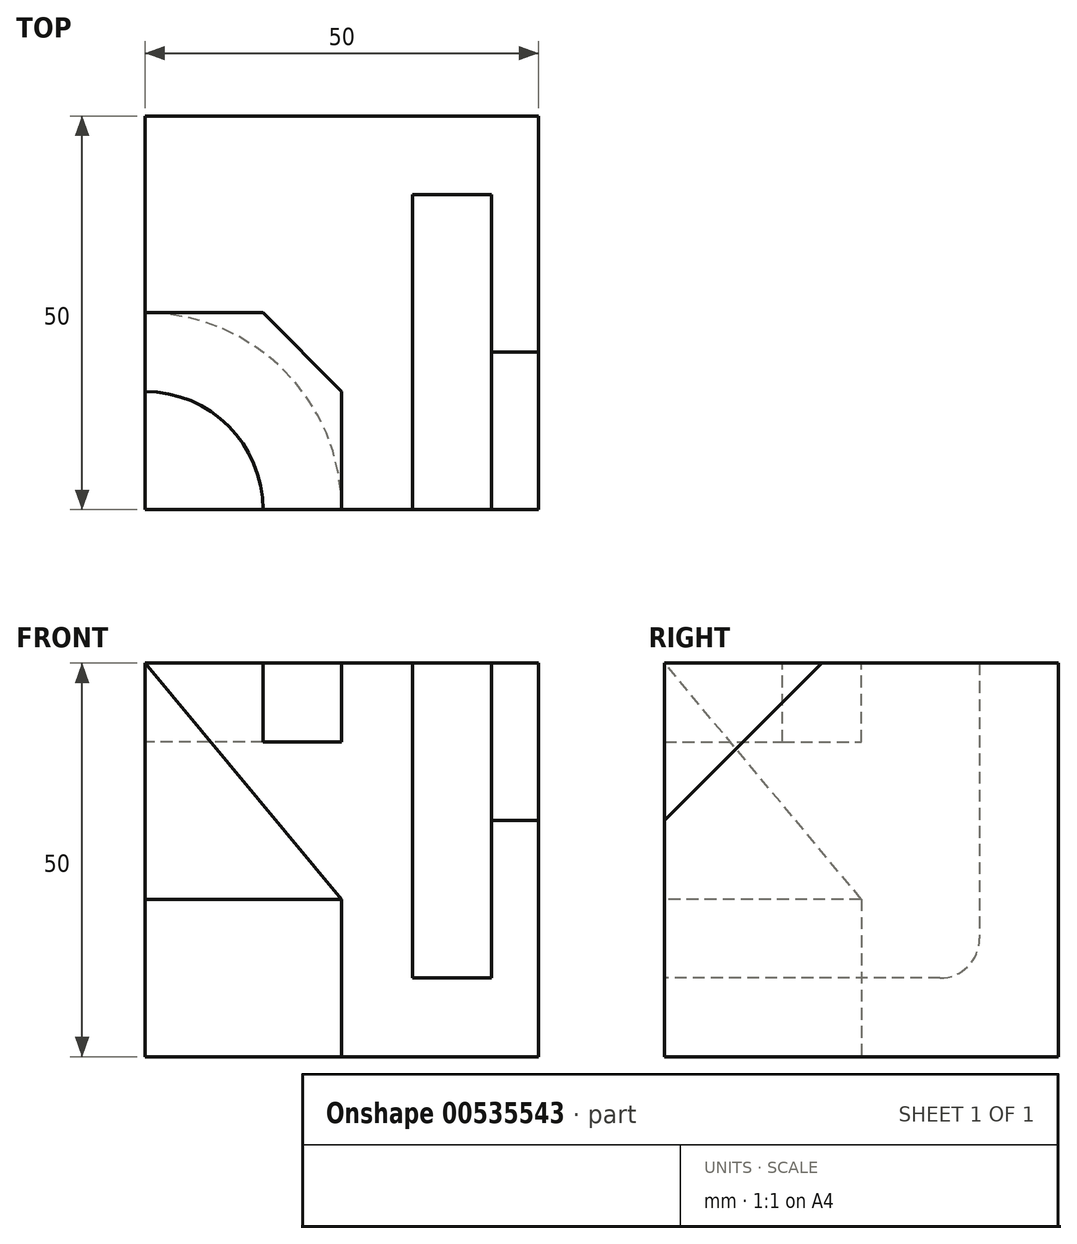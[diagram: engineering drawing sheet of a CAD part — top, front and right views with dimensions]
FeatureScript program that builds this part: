
annotation { "Feature Type Name" : "Feature", "Feature Type Description" : "" }
export const myFeature = defineFeature(function(context is Context, id is Id, definition is map)
    precondition{}
    {
        {
            var Q0;
            Q0=qCreatedBy(makeId("Front.planeOp"),FACE);
            var sketch = newSketch(context, id + "F0", { "sketchPlane" : qUnion([Q0])});
            skLineSegment(sketch, "E0.bottom", {"start": v(0, 0) * mm, "end": v(-50, 0) * mm});
            skLineSegment(sketch, "E0.top", {"start": v(0, 50) * mm, "end": v(-50, 50) * mm});
            skLineSegment(sketch, "E0.left", {"start": v(0, 0) * mm, "end": v(0, 50) * mm});
            skLineSegment(sketch, "E0.right", {"start": v(-50, 0) * mm, "end": v(-50, 50) * mm});
            skSolve(sketch);
        }
        {
            var Q0;
            Q0=makeQuery(id+"F0.imprint","IMPRINT",FACE,{"disambiguationData":[TD([[makeQuery(id+"F0.imprint","IMPRINT",EDGE,{"derivedFrom":sQuery(id+"F0.wireOp",EDGE,"E0.bottom")}),-1.0]])]});
            extrude(context, id + "F1", {"entities" : qUnion([Q0]), "depth" : 50 * mm, "offsetDistance" : 25 * mm});
        }
        {
            var Q0;
            Q0=makeQuery(id+"F1.opExtrude","SWEPT_FACE",FACE,{"disambiguationData":[OSD([sQuery(id+"F0.wireOp",EDGE,"E0.top")])]});
            var sketch = newSketch(context, id + "F2", { "sketchPlane" : qUnion([Q0])});
            skLineSegment(sketch, "E1", {"start": v(-50, -50) * mm, "end": v(-25, -50) * mm});
            skLineSegment(sketch, "E2", {"start": v(-25, -50) * mm, "end": v(-25, -35) * mm});
            skLineSegment(sketch, "E3", {"start": v(-25, -35) * mm, "end": v(-35, -25) * mm});
            skLineSegment(sketch, "E4", {"start": v(-35, -25) * mm, "end": v(-50, -25) * mm});
            skLineSegment(sketch, "E5", {"start": v(-50, -25) * mm, "end": v(-50, -50) * mm});
            skCircle(sketch, "E6", {"center": v(-50, -50) * mm, "radius": 15 * mm});
            skSolve(sketch);
        }
        {
            var Q0;
            {var subQ1=sQuery(id+"F2.wireOp",EDGE,"E2");Q0=makeQuery(id+"F2.imprint","IMPRINT",FACE,{"disambiguationData":[TD([[makeQuery(id+"F2.imprint","IMPRINT",EDGE,{"derivedFrom":subQ1}),1.0]])]});}
            extrude(context, id + "F3", {"entities" : qUnion([Q0]), "operationType" : NewBodyOperationType.REMOVE, "oppositeDirection" : true, "depth" : 10 * mm, "offsetDistance" : 25 * mm});
        }
        {
            var Q0;
            Q0=makeQuery(id+"F1.opExtrude","SWEPT_FACE",FACE,{"disambiguationData":[OSD([sQuery(id+"F0.wireOp",EDGE,"E0.bottom")])]});
            var sketch = newSketch(context, id + "F4", { "sketchPlane" : qUnion([Q0])});
            skCircle(sketch, "E7", {"center": v(-50, 50) * mm, "radius": 25 * mm});
            skSolve(sketch);
        }
        {
            var Q0;
            Q0=makeQuery(id+"F1.opExtrude","CAP_FACE",FACE,{"disambiguationData":[OSD([sQuery(id+"F0.wireOp",EDGE,"E0.bottom"),sQuery(id+"F0.wireOp",EDGE,"E0.top"),sQuery(id+"F0.wireOp",EDGE,"E0.left"),sQuery(id+"F0.wireOp",EDGE,"E0.right")])],"isStart":false});
            var sketch = newSketch(context, id + "F5", { "sketchPlane" : qUnion([Q0])});
            skLineSegment(sketch, "E8.bottom", {"start": v(-50, 0) * mm, "end": v(-25, 0) * mm});
            skLineSegment(sketch, "E8.top", {"start": v(-50, 20) * mm, "end": v(-25, 20) * mm});
            skLineSegment(sketch, "E8.left", {"start": v(-50, 0) * mm, "end": v(-50, 20) * mm});
            skLineSegment(sketch, "E8.right", {"start": v(-25, 0) * mm, "end": v(-25, 20) * mm});
            skSolve(sketch);
        }
        {
            var Q0;
            Q0=makeQuery(id+"F5.imprint","IMPRINT",FACE,{"disambiguationData":[TD([[makeQuery(id+"F5.imprint","IMPRINT",EDGE,{"derivedFrom":sQuery(id+"F5.wireOp",EDGE,"E8.bottom")}),-1.0]])]});
            var Q1;
            Q1=sQuery(id+"F4.wireOp",EDGE,"E7");
            sweep(context, id + "F6", {"operationType" : NewBodyOperationType.REMOVE, "profiles" : qUnion([Q0]), "path" : qUnion([Q1])});
        }
        {
            var Q0;
            Q0=makeQuery(id+"F1.opExtrude","CAP_FACE",FACE,{"disambiguationData":[OSD([sQuery(id+"F0.wireOp",EDGE,"E0.bottom"),sQuery(id+"F0.wireOp",EDGE,"E0.top"),sQuery(id+"F0.wireOp",EDGE,"E0.left"),sQuery(id+"F0.wireOp",EDGE,"E0.right")])],"isStart":false});
            var sketch = newSketch(context, id + "F7", { "sketchPlane" : qUnion([Q0])});
            skLineSegment(sketch, "E9", {"start": v(-50, 50) * mm, "end": v(-50, 20) * mm});
            skLineSegment(sketch, "E10", {"start": v(-50, 20) * mm, "end": v(-25, 20) * mm});
            skLineSegment(sketch, "E11", {"start": v(-25, 20) * mm, "end": v(-50, 50) * mm});
            skSolve(sketch);
        }
        {
            var Q0;
            Q0=makeQuery(id+"F7.imprint","IMPRINT",FACE,{"disambiguationData":[TD([[makeQuery(id+"F7.imprint","IMPRINT",EDGE,{"derivedFrom":sQuery(id+"F7.wireOp",EDGE,"E9")}),-1.0]])]});
            var Q1;
            Q1=makeQuery(id+"F6.boolean.opBoolean","COPY",EDGE,{"derivedFrom":makeQuery(id+"F6.opSweep","SWEPT_EDGE",EDGE,{"disambiguationData":[OSD([sQuery(id+"F4.wireOp",EDGE,"E7"),sQuery(id+"F5.wireOp",EDGE,"E8.top"),sQuery(id+"F5.wireOp",EDGE,"E8.right")])]})});
            sweep(context, id + "F8", {"operationType" : NewBodyOperationType.REMOVE, "profiles" : qUnion([Q0]), "path" : qUnion([Q1])});
        }
        {
            var Q0;
            Q0=makeQuery(id+"F1.opExtrude","SWEPT_FACE",FACE,{"disambiguationData":[OSD([sQuery(id+"F0.wireOp",EDGE,"E0.left")])]});
            var sketch = newSketch(context, id + "F9", { "sketchPlane" : qUnion([Q0])});
            skLineSegment(sketch, "E12.bottom", {"start": v(-50, 50) * mm, "end": v(-10, 50) * mm});
            skLineSegment(sketch, "E12.top", {"start": v(-50, 10) * mm, "end": v(-10, 10) * mm});
            skLineSegment(sketch, "E12.left", {"start": v(-50, 50) * mm, "end": v(-50, 10) * mm});
            skLineSegment(sketch, "E12.right", {"start": v(-10, 50) * mm, "end": v(-10, 10) * mm});
            skCircle(sketch, "E13", {"center": v(-15, 15) * mm, "radius": 5 * mm});
            skSolve(sketch);
        }
        {
            var Q0;
            {var subQ5=sQuery(id+"F5.wireOp",EDGE,"E8.top");Q0=makeQuery(id+"F5.imprint","IMPRINT",FACE,{"disambiguationData":[TD([[makeQuery(id+"F5.imprint","IMPRINT",EDGE,{"derivedFrom":subQ5}),1.0]])]});}
            var sketch = newSketch(context, id + "F10", { "sketchPlane" : qUnion([Q0])});
            skLineSegment(sketch, "E14.bottom", {"start": v(-16, 50) * mm, "end": v(-6, 50) * mm});
            skLineSegment(sketch, "E14.top", {"start": v(-16, 10) * mm, "end": v(-6, 10) * mm});
            skLineSegment(sketch, "E14.left", {"start": v(-16, 50) * mm, "end": v(-16, 10) * mm});
            skLineSegment(sketch, "E14.right", {"start": v(-6, 50) * mm, "end": v(-6, 10) * mm});
            skSolve(sketch);
        }
        {
            var Q0;
            Q0=makeQuery(id+"F10.imprint","IMPRINT",FACE,{"disambiguationData":[TD([[makeQuery(id+"F10.imprint","IMPRINT",EDGE,{"derivedFrom":sQuery(id+"F10.wireOp",EDGE,"E14.bottom")}),1.0]])]});
            extrude(context, id + "F11", {"entities" : qUnion([Q0]), "operationType" : NewBodyOperationType.REMOVE, "oppositeDirection" : true, "depth" : 40 * mm, "offsetDistance" : 25 * mm});
        }
        {
            var Q0;
            {var subQ0=sQuery(id+"F9.wireOp",EDGE,"E12.right");var subQ1=sQuery(id+"F9.wireOp",EDGE,"E12.top");var subQ2=makeQuery(id+"F9.imprint","INTERSECT",VERTEX,{"derivedFrom":[subQ1,subQ0]});Q0=makeQuery(id+"F9.imprint","IMPRINT",FACE,{"disambiguationData":[TD([[makeQuery(id+"F9.imprint","IMPRINT",EDGE,{"disambiguationData":[TD([[subQ2,1.0]])],"derivedFrom":subQ1}),1.0]])]});}
            extrude(context, id + "F12", {"entities" : qUnion([Q0]), "operationType" : NewBodyOperationType.ADD, "oppositeDirection" : true, "depth" : 16 * mm, "offsetDistance" : 25 * mm});
        }
        {
            var Q0;
            Q0=makeQuery(id+"F1.opExtrude","SWEPT_FACE",FACE,{"disambiguationData":[OSD([sQuery(id+"F0.wireOp",EDGE,"E0.left")])]});
            var sketch = newSketch(context, id + "F13", { "sketchPlane" : qUnion([Q0])});
            skLineSegment(sketch, "E15", {"start": v(-50, 50) * mm, "end": v(-50, 30) * mm});
            skLineSegment(sketch, "E16", {"start": v(-50, 30) * mm, "end": v(-30, 50) * mm});
            skLineSegment(sketch, "E17", {"start": v(-30, 50) * mm, "end": v(-50, 50) * mm});
            skSolve(sketch);
        }
        {
            var Q0;
            Q0=makeQuery(id+"F13.imprint","IMPRINT",FACE,{"disambiguationData":[TD([[makeQuery(id+"F13.imprint","IMPRINT",EDGE,{"derivedFrom":sQuery(id+"F13.wireOp",EDGE,"E15")}),-1.0]])]});
            extrude(context, id + "F14", {"entities" : qUnion([Q0]), "operationType" : NewBodyOperationType.REMOVE, "oppositeDirection" : true, "depth" : 6 * mm, "offsetDistance" : 25 * mm});
        }
    });
